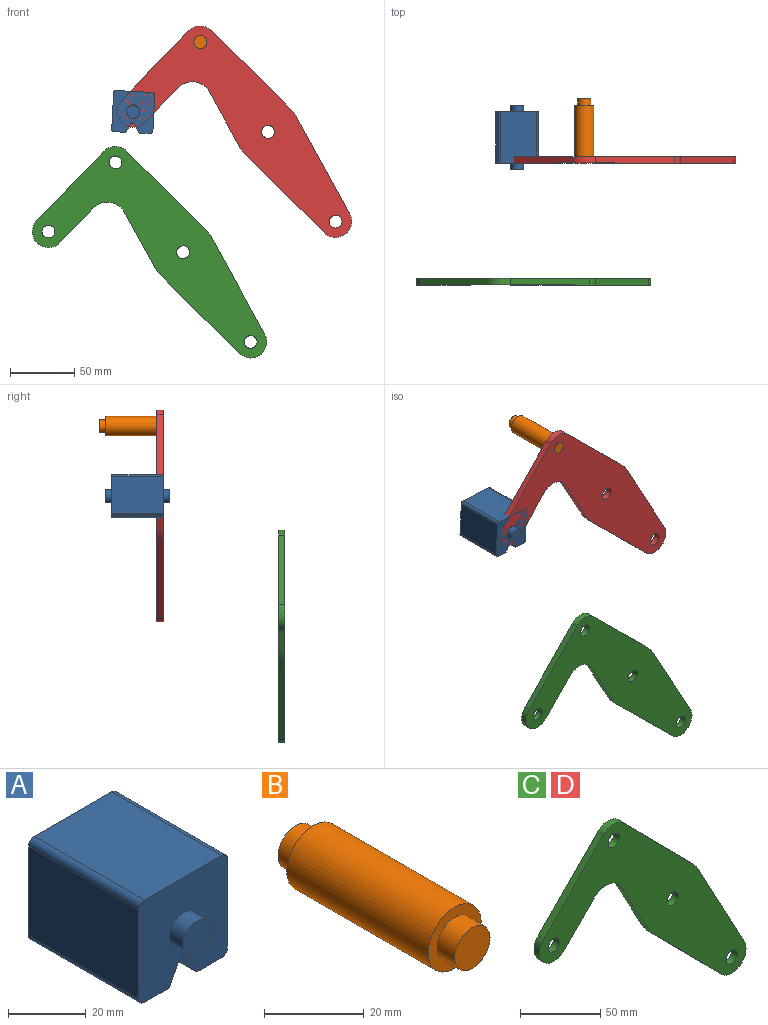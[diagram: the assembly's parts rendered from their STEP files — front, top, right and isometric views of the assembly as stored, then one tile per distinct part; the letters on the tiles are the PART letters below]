
ASSEMBLY  parts=4 mates=1
PART A: 18 faces, bbox 32.1x50x32.1 mm
  f0: plane 40x28.08mm, normal (1,0,0), area 1123.1mm2, adj f4,f10,f13,f14
  f1: plane 40x9.04mm, normal (0,0,-1), area 361.6mm2, adj f2,f4,f10,f14
  f2: plane 40x6.42mm, normal (-0.89,0,-0.45), area 287.2mm2, adj f1,f4,f10,f15
  f3: plane 40x6.42mm, normal (0.89,0,-0.45), area 287.2mm2, adj f4,f5,f10,f15
  f4: plane 32.08x32.08mm, normal (0,-1,0), area 900.6mm2, adj f0,f1,f2,f3,f5,f6,f7,f9
  f5: plane 40x9.04mm, normal (0,0,-1), area 361.6mm2, adj f3,f4,f10,f16
  f6: plane 40x28.08mm, normal (0,0,1), area 1123.1mm2, adj f4,f10,f13,f17
  f7: plane 40x28.08mm, normal (-1,0,0), area 1123.1mm2, adj f4,f10,f16,f17
  f8: plane 10x10mm, normal (0,-1,0), area 78.5mm2, adj f9
  f9: cylinder r=5mm len=10mm, axis (0,1,0), area 157.1mm2, adj f4,f8
  f10: plane 32.08x32.08mm, normal (0,1,0), area 900.6mm2, adj f0,f1,f2,f3,f5,f6,f7,f12
  f11: plane 10x10mm, normal (0,1,0), area 78.5mm2, adj f12
  f12: cylinder r=5mm len=10mm, axis (0,-1,0), area 157.1mm2, adj f10,f11
  f13: cylinder r=2mm len=40mm, axis (0,1,0), area 125.7mm2, adj f0,f4,f6,f10
  f14: cylinder r=2mm len=40mm, axis (0,-1,0), area 125.7mm2, adj f0,f1,f4,f10
  f15: cylinder r=2mm len=40mm, axis (0,1,0), area 177.1mm2, adj f2,f3,f4,f10
  f16: cylinder r=2mm len=40mm, axis (0,1,0), area 125.7mm2, adj f4,f5,f7,f10
  f17: cylinder r=2mm len=40mm, axis (0,-1,0), area 125.7mm2, adj f4,f6,f7,f10
PART B: 7 faces, bbox 15x50x15 mm
  f0: cylinder r=7.5mm len=40mm, axis (0,-1,0), area 1885mm2, adj f2,f5
  f1: cylinder r=5mm len=10mm, axis (0,1,0), area 157.1mm2, adj f2,f3
  f2: plane 15x15mm, normal (0,-1,0), area 98.2mm2, adj f0,f1
  f3: plane 10x10mm, normal (0,-1,0), area 78.5mm2, adj f1
  f4: cylinder r=5mm len=10mm, axis (0,-1,0), area 157.1mm2, adj f5,f6
  f5: plane 15x15mm, normal (0,1,0), area 98.2mm2, adj f0,f4
  f6: plane 10x10mm, normal (0,1,0), area 78.5mm2, adj f4
PART C: 18 faces, bbox 181.7x5x165.8 mm
  f0: plane 43.49x23.35mm, normal (-0.88,0,-0.47), area 246.8mm2, adj f1,f14,f16,f17
  f1: cylinder r=25mm len=5.75mm, axis (0,1,0), area 35.8mm2, adj f0,f2,f16,f17
  f2: plane 61.6x60.87mm, normal (-0.71,0,-0.7), area 433mm2, adj f1,f3,f16,f17
  f3: cylinder r=12.5mm len=21.39mm, axis (0,1,0), area 178.4mm2, adj f2,f4,f16,f17
  f4: plane 76.3x40.96mm, normal (0.88,0,0.47), area 433mm2, adj f3,f5,f16,f17
  f5: cylinder r=25mm len=5.75mm, axis (0,1,0), area 35.8mm2, adj f4,f6,f16,f17
  f6: plane 61.6x60.87mm, normal (0.71,0,0.7), area 433mm2, adj f5,f7,f16,f17
  f7: cylinder r=12.5mm len=17.78mm, axis (0,1,0), area 98.9mm2, adj f6,f8,f16,f17
  f8: plane 53.35x52.71mm, normal (-0.71,0,0.7), area 375mm2, adj f7,f9,f16,f17
  f9: cylinder r=12.5mm len=21.39mm, axis (0,1,0), area 196.3mm2, adj f8,f10,f16,f17
  f10: plane 26.86x26.54mm, normal (0.71,0,-0.7), area 188.8mm2, adj f9,f14,f16,f17
  f11: cylinder r=5mm len=10mm, axis (0,1,0), area 157.1mm2, adj f16,f17
  f12: cylinder r=5mm len=10mm, axis (0,1,0), area 157.1mm2, adj f16,f17
  f13: cylinder r=5mm len=10mm, axis (0,1,0), area 157.1mm2, adj f16,f17
  f14: cylinder r=15mm len=23.89mm, axis (0,1,0), area 140.2mm2, adj f0,f10,f16,f17
  f15: cylinder r=5mm len=10mm, axis (0,1,0), area 157.1mm2, adj f16,f17
  f16: plane 181.66x165.78mm, normal (0,-1,0), area 8710.1mm2, adj f0,f1,f2,f3,f4,f5,f6,f7
  f17: plane 181.66x165.78mm, normal (0,1,0), area 8710.1mm2, adj f0,f1,f2,f3,f4,f5,f6,f7
PART D: same geometry as C
PLACE A rot(axis=(0,1,0),3deg) t=(12.8,29.98,61.4)mm
PLACE B rot(axis=(0,-1,0),0.5deg) t=(14.02,34.98,68.47)mm
PLACE C rot(axis=(0,-1,0),0.5deg) t=(-52.07,-59.77,-25.24)mm
PLACE D rot(axis=(0,-1,0),0.5deg) t=(14.02,34.98,68.47)mm fixed
MATE revolute A.f4 <-> D.f9  axis (0,-1,0) through (-90.83,29.98,84.51)mm
